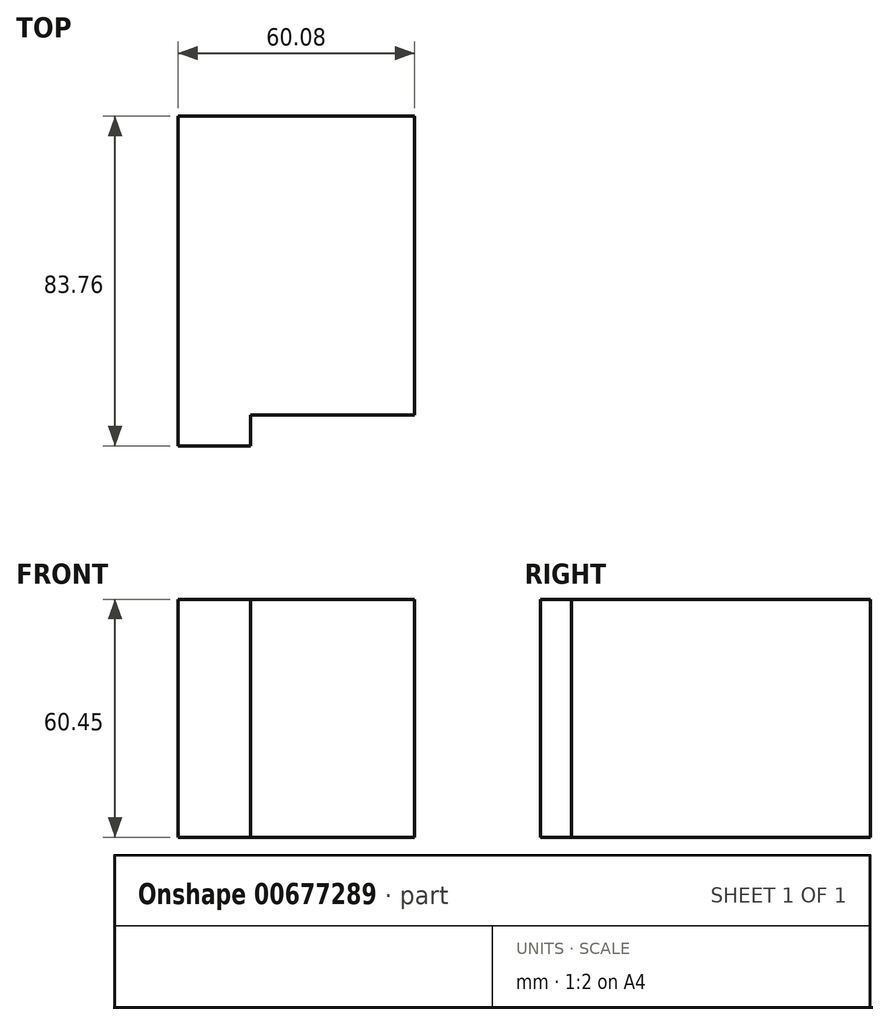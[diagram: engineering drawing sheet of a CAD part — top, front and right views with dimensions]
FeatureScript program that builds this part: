
annotation { "Feature Type Name" : "Feature", "Feature Type Description" : "" }
export const myFeature = defineFeature(function(context is Context, id is Id, definition is map)
    precondition{}
    {
        {
            var Q0;
            Q0=qCreatedBy(makeId("Top.planeOp"),FACE);
            var sketch = newSketch(context, id + "F0", { "sketchPlane" : qUnion([Q0])});
            skLineSegment(sketch, "E0.bottom", {"start": v(-151.78, 22.5) * mm, "end": v(-91.7, 22.5) * mm});
            skLineSegment(sketch, "E0.top", {"start": v(-151.78, -53.45) * mm, "end": v(-91.7, -53.45) * mm});
            skLineSegment(sketch, "E0.left", {"start": v(-151.78, 22.5) * mm, "end": v(-151.78, -53.45) * mm});
            skLineSegment(sketch, "E0.right", {"start": v(-91.7, 22.5) * mm, "end": v(-91.7, -53.45) * mm});
            skLineSegment(sketch, "E1.bottom", {"start": v(-151.78, -53.45) * mm, "end": v(-133.37, -53.45) * mm});
            skLineSegment(sketch, "E1.top", {"start": v(-151.78, -61.27) * mm, "end": v(-133.37, -61.27) * mm});
            skLineSegment(sketch, "E1.left", {"start": v(-151.78, -53.45) * mm, "end": v(-151.78, -61.27) * mm});
            skLineSegment(sketch, "E1.right", {"start": v(-133.37, -53.45) * mm, "end": v(-133.37, -61.27) * mm});
            skSolve(sketch);
        }
        {
            var Q0;
            Q0 = qSketchRegion(id + "F0", true);
            extrude(context, id + "F1", {"entities" : qUnion([Q0]), "depth" : 60.45 * mm, "offsetDistance" : 25.4 * mm});
        }
    });
